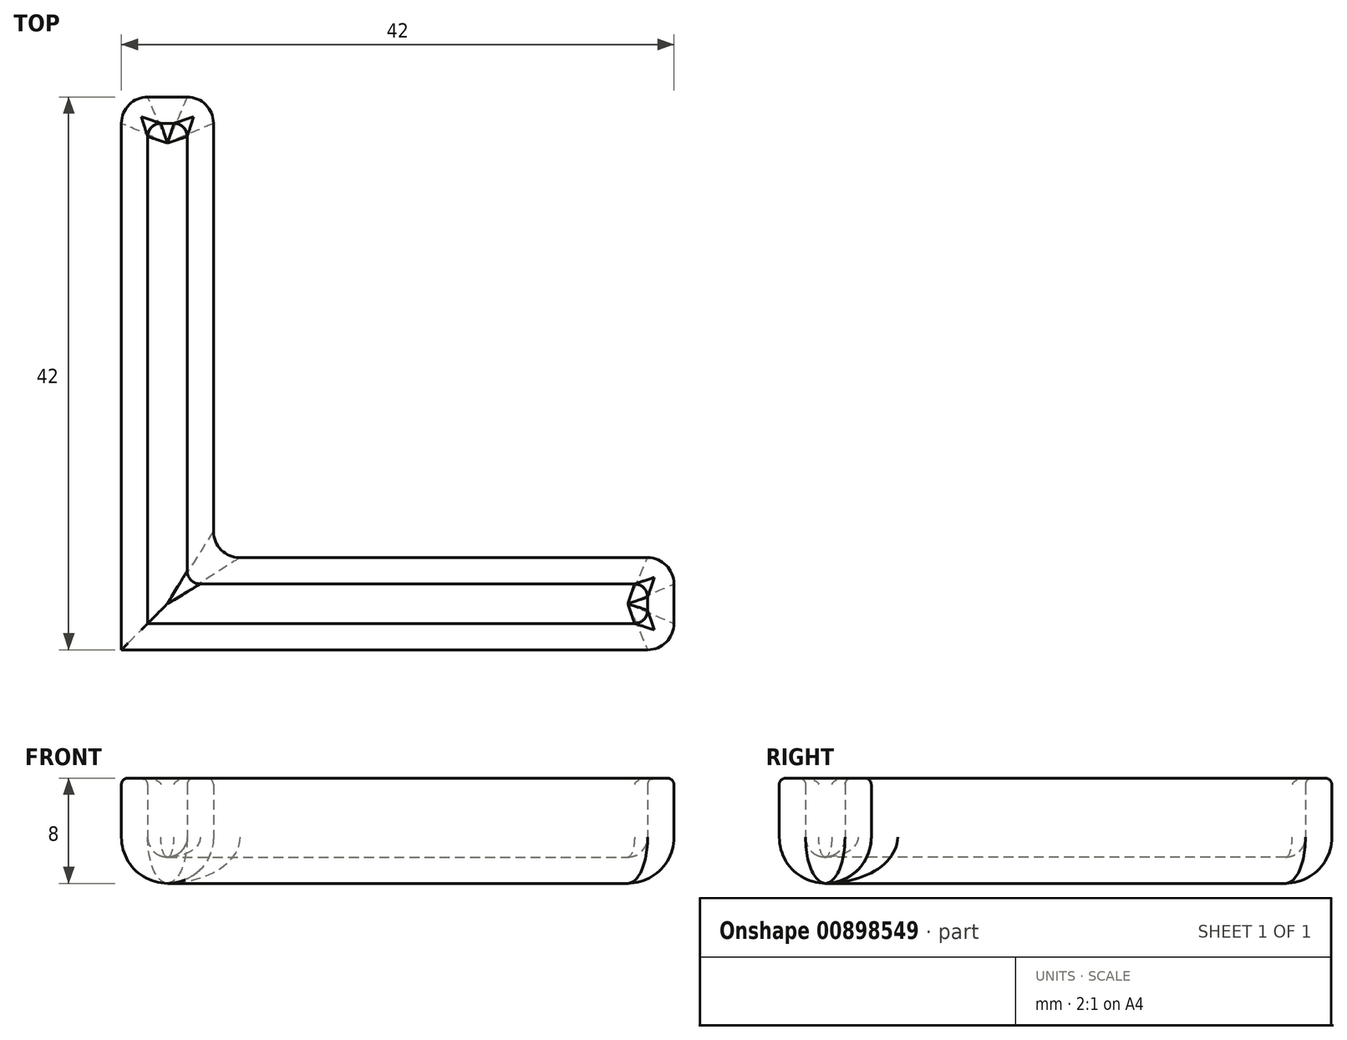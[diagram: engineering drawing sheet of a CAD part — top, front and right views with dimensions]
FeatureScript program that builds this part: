
annotation { "Feature Type Name" : "Feature", "Feature Type Description" : "" }
export const myFeature = defineFeature(function(context is Context, id is Id, definition is map)
    precondition{}
    {
        {
            var Q0;
            Q0=qCreatedBy(makeId("Top.planeOp"),FACE);
            var sketch = newSketch(context, id + "F0", { "sketchPlane" : qUnion([Q0])});
            skLineSegment(sketch, "E0.bottom", {"start": v(0.08, 0.3) * mm, "end": v(42.08, 0.3) * mm});
            skLineSegment(sketch, "E0.top", {"start": v(7.08, 7.3) * mm, "end": v(42.08, 7.3) * mm});
            skLineSegment(sketch, "E0.left", {"start": v(0.08, 0.3) * mm, "end": v(0.08, 7.3) * mm});
            skLineSegment(sketch, "E0.right", {"start": v(42.08, 0.3) * mm, "end": v(42.08, 7.3) * mm});
            skLineSegment(sketch, "E1.bottom", {"start": v(0.08, 0.3) * mm, "end": v(7.08, 0.3) * mm});
            skLineSegment(sketch, "E1.top", {"start": v(0.08, 42.3) * mm, "end": v(7.08, 42.3) * mm});
            skLineSegment(sketch, "E1.left", {"start": v(0.08, 0.3) * mm, "end": v(0.08, 42.3) * mm});
            skLineSegment(sketch, "E1.right", {"start": v(7.08, 7.3) * mm, "end": v(7.08, 42.3) * mm});
            skSolve(sketch);
        }
        {
            var Q0;
            Q0=makeQuery(id+"F0.imprint","IMPRINT",FACE,{"disambiguationData":[TD([[makeQuery(id+"F0.imprint","IMPRINT",EDGE,{"derivedFrom":sQuery(id+"F0.wireOp",EDGE,"E0.bottom")}),1.0]])]});
            extrude(context, id + "F1", {"entities" : qUnion([Q0]), "depth" : 6 * mm, "offsetDistance" : 25 * mm});
        }
        {
            var Q0;
            Q0=makeQuery(id+"F1.opExtrude","CAP_FACE",FACE,{"disambiguationData":[OSD([sQuery(id+"F0.wireOp",EDGE,"E0.bottom"),sQuery(id+"F0.wireOp",EDGE,"E0.top"),sQuery(id+"F0.wireOp",EDGE,"E0.right"),sQuery(id+"F0.wireOp",EDGE,"E1.bottom"),sQuery(id+"F0.wireOp",EDGE,"E1.top"),sQuery(id+"F0.wireOp",EDGE,"E1.left"),sQuery(id+"F0.wireOp",EDGE,"E1.right")])],"isStart":true});
            extrude(context, id + "F2", {"entities" : qUnion([Q0]), "operationType" : NewBodyOperationType.ADD, "depth" : 2 * mm, "offsetDistance" : 25 * mm});
        }
        {
            var Q0;
            Q0=makeQuery(id+"F2.opExtrude","CAP_EDGE",EDGE,{"disambiguationData":[OSD([sQuery(id+"F0.wireOp",EDGE,"E1.left")])],"isStart":false});
            var Q1;
            Q1=makeQuery(id+"F2.opExtrude","CAP_EDGE",EDGE,{"disambiguationData":[OSD([sQuery(id+"F0.wireOp",EDGE,"E1.top")])],"isStart":false});
            var Q2;
            Q2=makeQuery(id+"F2.opExtrude","CAP_EDGE",EDGE,{"disambiguationData":[OSD([sQuery(id+"F0.wireOp",EDGE,"E1.right")])],"isStart":false});
            var Q3;
            Q3=makeQuery(id+"F2.opExtrude","CAP_EDGE",EDGE,{"disambiguationData":[OSD([sQuery(id+"F0.wireOp",EDGE,"E0.top")])],"isStart":false});
            var Q4;
            Q4=makeQuery(id+"F2.opExtrude","CAP_EDGE",EDGE,{"disambiguationData":[OSD([sQuery(id+"F0.wireOp",EDGE,"E0.bottom"),sQuery(id+"F0.wireOp",EDGE,"E1.bottom")])],"isStart":false});
            var Q5;
            Q5=makeQuery(id+"F2.opExtrude","CAP_EDGE",EDGE,{"disambiguationData":[OSD([sQuery(id+"F0.wireOp",EDGE,"E0.right")])],"isStart":false});
            fillet(context, id + "F3", {"entities" : qUnion([Q0, Q1, Q2, Q3, Q4, Q5]), "radius" : 3.5 * mm, "tangentPropagation" : true, "allowEdgeOverflow" : false});
        }
        {
            var Q0;
            Q0=makeQuery(id+"F1.opExtrude","CAP_FACE",FACE,{"disambiguationData":[OSD([sQuery(id+"F0.wireOp",EDGE,"E0.bottom"),sQuery(id+"F0.wireOp",EDGE,"E0.top"),sQuery(id+"F0.wireOp",EDGE,"E0.right"),sQuery(id+"F0.wireOp",EDGE,"E1.bottom"),sQuery(id+"F0.wireOp",EDGE,"E1.top"),sQuery(id+"F0.wireOp",EDGE,"E1.left"),sQuery(id+"F0.wireOp",EDGE,"E1.right")])],"isStart":false});
            shell(context, id + "F4", {"entities" : qUnion([Q0]), "thickness" : 2 * mm});
        }
        {
            var Q0;
            {var subQ0=sQuery(id+"F0.wireOp",EDGE,"E0.right");var subQ1=sQuery(id+"F0.wireOp",EDGE,"E0.top");Q0=makeQuery(id+"F2.boolean.opBoolean","MERGE",EDGE,{"derivedFrom":[makeQuery(id+"F1.opExtrude","SWEPT_EDGE",EDGE,{"disambiguationData":[OSD([subQ1,subQ0])]}),makeQuery(id+"F2.opExtrude","SWEPT_EDGE",EDGE,{"disambiguationData":[OSD([subQ1,subQ0])]})]});}
            var Q1;
            {var subQ0=sQuery(id+"F0.wireOp",EDGE,"E0.right");var subQ1=sQuery(id+"F0.wireOp",EDGE,"E0.bottom");Q1=makeQuery(id+"F2.boolean.opBoolean","MERGE",EDGE,{"derivedFrom":[makeQuery(id+"F1.opExtrude","SWEPT_EDGE",EDGE,{"disambiguationData":[OSD([subQ1,subQ0])]}),makeQuery(id+"F2.opExtrude","SWEPT_EDGE",EDGE,{"disambiguationData":[OSD([subQ1,subQ0])]})]});}
            var Q2;
            {var subQ0=sQuery(id+"F0.wireOp",EDGE,"E1.left");var subQ1=sQuery(id+"F0.wireOp",EDGE,"E1.bottom");Q2=makeQuery(id+"F2.boolean.opBoolean","MERGE",EDGE,{"derivedFrom":[makeQuery(id+"F1.opExtrude","SWEPT_EDGE",EDGE,{"disambiguationData":[OSD([subQ1,subQ0])]}),makeQuery(id+"F2.opExtrude","SWEPT_EDGE",EDGE,{"disambiguationData":[OSD([subQ1,subQ0])]})]});}
            var Q3;
            {var subQ0=sQuery(id+"F0.wireOp",EDGE,"E1.right");var subQ1=sQuery(id+"F0.wireOp",EDGE,"E0.top");Q3=makeQuery(id+"F2.boolean.opBoolean","MERGE",EDGE,{"derivedFrom":[makeQuery(id+"F1.opExtrude","SWEPT_EDGE",EDGE,{"disambiguationData":[OSD([subQ1,subQ0])]}),makeQuery(id+"F2.opExtrude","SWEPT_EDGE",EDGE,{"disambiguationData":[OSD([subQ1,subQ0])]})]});}
            var Q4;
            {var subQ0=sQuery(id+"F0.wireOp",EDGE,"E1.right");var subQ1=sQuery(id+"F0.wireOp",EDGE,"E1.top");Q4=makeQuery(id+"F2.boolean.opBoolean","MERGE",EDGE,{"derivedFrom":[makeQuery(id+"F1.opExtrude","SWEPT_EDGE",EDGE,{"disambiguationData":[OSD([subQ1,subQ0])]}),makeQuery(id+"F2.opExtrude","SWEPT_EDGE",EDGE,{"disambiguationData":[OSD([subQ1,subQ0])]})]});}
            var Q5;
            {var subQ0=sQuery(id+"F0.wireOp",EDGE,"E1.left");var subQ1=sQuery(id+"F0.wireOp",EDGE,"E1.top");Q5=makeQuery(id+"F2.boolean.opBoolean","MERGE",EDGE,{"derivedFrom":[makeQuery(id+"F1.opExtrude","SWEPT_EDGE",EDGE,{"disambiguationData":[OSD([subQ1,subQ0])]}),makeQuery(id+"F2.opExtrude","SWEPT_EDGE",EDGE,{"disambiguationData":[OSD([subQ1,subQ0])]})]});}
            fillet(context, id + "F5", {"entities" : qUnion([Q0, Q1, Q2, Q3, Q4, Q5]), "radius" : 2 * mm, "tangentPropagation" : true, "allowEdgeOverflow" : false});
        }
        {
            var Q0;
            {var subQ0=sQuery(id+"F0.wireOp",EDGE,"E1.bottom");var subQ1=sQuery(id+"F0.wireOp",EDGE,"E0.bottom");Q0=makeQuery(id+"F4.opShell","OFFSET_EDGE",EDGE,{"disambiguationData":[OSD([subQ1,subQ0]),TDD([makeQuery(id+"F1.opExtrude","CAP_EDGE",EDGE,{"disambiguationData":[OSD([subQ1,subQ0])],"isStart":false})])]});}
            var Q1;
            {var subQ0=sQuery(id+"F0.wireOp",EDGE,"E1.left");var subQ1=sQuery(id+"F0.wireOp",EDGE,"E1.bottom");Q1=makeQuery(id+"FFNLwZtD0nWtF8N_1.opFillet","BLEND_EDGE",EDGE,{"blendedFrom":[makeQuery(id+"F4.opShell","OFFSET_EDGE",EDGE,{"disambiguationData":[OSD([subQ1,subQ0])]}),makeQuery(id+"F1.opExtrude","CAP_FACE",FACE,{"disambiguationData":[OSD([sQuery(id+"F0.wireOp",EDGE,"E0.bottom"),sQuery(id+"F0.wireOp",EDGE,"E0.top"),sQuery(id+"F0.wireOp",EDGE,"E0.right"),subQ1,sQuery(id+"F0.wireOp",EDGE,"E1.top"),subQ0,sQuery(id+"F0.wireOp",EDGE,"E1.right")])],"isStart":false})],"blendedInto":[makeQuery(id+"F1.opExtrude","CAP_FACE",FACE,{"disambiguationData":[OSD([sQuery(id+"F0.wireOp",EDGE,"E0.bottom"),sQuery(id+"F0.wireOp",EDGE,"E0.top"),sQuery(id+"F0.wireOp",EDGE,"E0.right"),subQ1,sQuery(id+"F0.wireOp",EDGE,"E1.top"),subQ0,sQuery(id+"F0.wireOp",EDGE,"E1.right")])],"isStart":false})]});}
            var Q2;
            {var subQ0=sQuery(id+"F0.wireOp",EDGE,"E1.left");Q2=makeQuery(id+"F4.opShell","OFFSET_EDGE",EDGE,{"disambiguationData":[OSD([subQ0]),TDD([makeQuery(id+"F1.opExtrude","CAP_EDGE",EDGE,{"disambiguationData":[OSD([subQ0])],"isStart":false})])]});}
            var Q3;
            {var subQ0=sQuery(id+"F0.wireOp",EDGE,"E1.right");Q3=makeQuery(id+"F4.opShell","OFFSET_EDGE",EDGE,{"disambiguationData":[OSD([subQ0]),TDD([makeQuery(id+"F1.opExtrude","CAP_EDGE",EDGE,{"disambiguationData":[OSD([subQ0])],"isStart":false})])]});}
            var Q4;
            {var subQ0=sQuery(id+"F0.wireOp",EDGE,"E1.right");var subQ1=sQuery(id+"F0.wireOp",EDGE,"E0.top");Q4=makeQuery(id+"FFNLwZtD0nWtF8N_1.opFillet","BLEND_EDGE",EDGE,{"blendedFrom":[makeQuery(id+"F4.opShell","OFFSET_EDGE",EDGE,{"disambiguationData":[OSD([subQ1,subQ0])]}),makeQuery(id+"F1.opExtrude","CAP_FACE",FACE,{"disambiguationData":[OSD([sQuery(id+"F0.wireOp",EDGE,"E0.bottom"),subQ1,sQuery(id+"F0.wireOp",EDGE,"E0.right"),sQuery(id+"F0.wireOp",EDGE,"E1.bottom"),sQuery(id+"F0.wireOp",EDGE,"E1.top"),sQuery(id+"F0.wireOp",EDGE,"E1.left"),subQ0])],"isStart":false})],"blendedInto":[makeQuery(id+"F1.opExtrude","CAP_FACE",FACE,{"disambiguationData":[OSD([sQuery(id+"F0.wireOp",EDGE,"E0.bottom"),subQ1,sQuery(id+"F0.wireOp",EDGE,"E0.right"),sQuery(id+"F0.wireOp",EDGE,"E1.bottom"),sQuery(id+"F0.wireOp",EDGE,"E1.top"),sQuery(id+"F0.wireOp",EDGE,"E1.left"),subQ0])],"isStart":false})]});}
            var Q5;
            {var subQ0=sQuery(id+"F0.wireOp",EDGE,"E0.top");Q5=makeQuery(id+"F4.opShell","OFFSET_EDGE",EDGE,{"disambiguationData":[OSD([subQ0]),TDD([makeQuery(id+"F1.opExtrude","CAP_EDGE",EDGE,{"disambiguationData":[OSD([subQ0])],"isStart":false})])]});}
            var Q6;
            {var subQ0=sQuery(id+"F0.wireOp",EDGE,"E0.right");var subQ1=sQuery(id+"F0.wireOp",EDGE,"E0.top");Q6=makeQuery(id+"FFNLwZtD0nWtF8N_1.opFillet","BLEND_EDGE",EDGE,{"blendedFrom":[makeQuery(id+"F4.opShell","OFFSET_EDGE",EDGE,{"disambiguationData":[OSD([subQ1,subQ0]),TDD([makeQuery(id+"F2.boolean.opBoolean","MERGE",EDGE,{"derivedFrom":[makeQuery(id+"F1.opExtrude","SWEPT_EDGE",EDGE,{"disambiguationData":[OSD([subQ1,subQ0])]}),makeQuery(id+"F2.opExtrude","SWEPT_EDGE",EDGE,{"disambiguationData":[OSD([subQ1,subQ0])]})]})])]}),makeQuery(id+"F1.opExtrude","CAP_FACE",FACE,{"disambiguationData":[OSD([sQuery(id+"F0.wireOp",EDGE,"E0.bottom"),subQ1,subQ0,sQuery(id+"F0.wireOp",EDGE,"E1.bottom"),sQuery(id+"F0.wireOp",EDGE,"E1.top"),sQuery(id+"F0.wireOp",EDGE,"E1.left"),sQuery(id+"F0.wireOp",EDGE,"E1.right")])],"isStart":false})],"blendedInto":[makeQuery(id+"F1.opExtrude","CAP_FACE",FACE,{"disambiguationData":[OSD([sQuery(id+"F0.wireOp",EDGE,"E0.bottom"),subQ1,subQ0,sQuery(id+"F0.wireOp",EDGE,"E1.bottom"),sQuery(id+"F0.wireOp",EDGE,"E1.top"),sQuery(id+"F0.wireOp",EDGE,"E1.left"),sQuery(id+"F0.wireOp",EDGE,"E1.right")])],"isStart":false})]});}
            var Q7;
            {var subQ0=sQuery(id+"F0.wireOp",EDGE,"E0.right");var subQ1=sQuery(id+"F0.wireOp",EDGE,"E0.bottom");Q7=makeQuery(id+"FFNLwZtD0nWtF8N_1.opFillet","BLEND_EDGE",EDGE,{"blendedFrom":[makeQuery(id+"F4.opShell","OFFSET_EDGE",EDGE,{"disambiguationData":[OSD([subQ1,subQ0])]}),makeQuery(id+"F1.opExtrude","CAP_FACE",FACE,{"disambiguationData":[OSD([subQ1,sQuery(id+"F0.wireOp",EDGE,"E0.top"),subQ0,sQuery(id+"F0.wireOp",EDGE,"E1.bottom"),sQuery(id+"F0.wireOp",EDGE,"E1.top"),sQuery(id+"F0.wireOp",EDGE,"E1.left"),sQuery(id+"F0.wireOp",EDGE,"E1.right")])],"isStart":false})],"blendedInto":[makeQuery(id+"F1.opExtrude","CAP_FACE",FACE,{"disambiguationData":[OSD([subQ1,sQuery(id+"F0.wireOp",EDGE,"E0.top"),subQ0,sQuery(id+"F0.wireOp",EDGE,"E1.bottom"),sQuery(id+"F0.wireOp",EDGE,"E1.top"),sQuery(id+"F0.wireOp",EDGE,"E1.left"),sQuery(id+"F0.wireOp",EDGE,"E1.right")])],"isStart":false})]});}
            var Q8;
            {var subQ0=sQuery(id+"F0.wireOp",EDGE,"E0.right");Q8=makeQuery(id+"F4.opShell","OFFSET_EDGE",EDGE,{"disambiguationData":[OSD([subQ0]),TDD([makeQuery(id+"F1.opExtrude","CAP_EDGE",EDGE,{"disambiguationData":[OSD([subQ0])],"isStart":false})])]});}
            var Q9;
            {var subQ0=sQuery(id+"F0.wireOp",EDGE,"E1.left");var subQ1=sQuery(id+"F0.wireOp",EDGE,"E1.top");Q9=makeQuery(id+"FFNLwZtD0nWtF8N_1.opFillet","BLEND_EDGE",EDGE,{"blendedFrom":[makeQuery(id+"F4.opShell","OFFSET_EDGE",EDGE,{"disambiguationData":[OSD([subQ1,subQ0]),TDD([makeQuery(id+"F2.boolean.opBoolean","MERGE",EDGE,{"derivedFrom":[makeQuery(id+"F1.opExtrude","SWEPT_EDGE",EDGE,{"disambiguationData":[OSD([subQ1,subQ0])]}),makeQuery(id+"F2.opExtrude","SWEPT_EDGE",EDGE,{"disambiguationData":[OSD([subQ1,subQ0])]})]})])]}),makeQuery(id+"F1.opExtrude","CAP_FACE",FACE,{"disambiguationData":[OSD([sQuery(id+"F0.wireOp",EDGE,"E0.bottom"),sQuery(id+"F0.wireOp",EDGE,"E0.top"),sQuery(id+"F0.wireOp",EDGE,"E0.right"),sQuery(id+"F0.wireOp",EDGE,"E1.bottom"),subQ1,subQ0,sQuery(id+"F0.wireOp",EDGE,"E1.right")])],"isStart":false})],"blendedInto":[makeQuery(id+"F1.opExtrude","CAP_FACE",FACE,{"disambiguationData":[OSD([sQuery(id+"F0.wireOp",EDGE,"E0.bottom"),sQuery(id+"F0.wireOp",EDGE,"E0.top"),sQuery(id+"F0.wireOp",EDGE,"E0.right"),sQuery(id+"F0.wireOp",EDGE,"E1.bottom"),subQ1,subQ0,sQuery(id+"F0.wireOp",EDGE,"E1.right")])],"isStart":false})]});}
            var Q10;
            {var subQ0=sQuery(id+"F0.wireOp",EDGE,"E1.top");Q10=makeQuery(id+"F4.opShell","OFFSET_EDGE",EDGE,{"disambiguationData":[OSD([subQ0]),TDD([makeQuery(id+"F1.opExtrude","CAP_EDGE",EDGE,{"disambiguationData":[OSD([subQ0])],"isStart":false})])]});}
            var Q11;
            {var subQ0=sQuery(id+"F0.wireOp",EDGE,"E1.right");var subQ1=sQuery(id+"F0.wireOp",EDGE,"E1.top");Q11=makeQuery(id+"FFNLwZtD0nWtF8N_1.opFillet","BLEND_EDGE",EDGE,{"blendedFrom":[makeQuery(id+"F4.opShell","OFFSET_EDGE",EDGE,{"disambiguationData":[OSD([subQ1,subQ0]),TDD([makeQuery(id+"F2.boolean.opBoolean","MERGE",EDGE,{"derivedFrom":[makeQuery(id+"F1.opExtrude","SWEPT_EDGE",EDGE,{"disambiguationData":[OSD([subQ1,subQ0])]}),makeQuery(id+"F2.opExtrude","SWEPT_EDGE",EDGE,{"disambiguationData":[OSD([subQ1,subQ0])]})]})])]}),makeQuery(id+"F1.opExtrude","CAP_FACE",FACE,{"disambiguationData":[OSD([sQuery(id+"F0.wireOp",EDGE,"E0.bottom"),sQuery(id+"F0.wireOp",EDGE,"E0.top"),sQuery(id+"F0.wireOp",EDGE,"E0.right"),sQuery(id+"F0.wireOp",EDGE,"E1.bottom"),subQ1,sQuery(id+"F0.wireOp",EDGE,"E1.left"),subQ0])],"isStart":false})],"blendedInto":[makeQuery(id+"F1.opExtrude","CAP_FACE",FACE,{"disambiguationData":[OSD([sQuery(id+"F0.wireOp",EDGE,"E0.bottom"),sQuery(id+"F0.wireOp",EDGE,"E0.top"),sQuery(id+"F0.wireOp",EDGE,"E0.right"),sQuery(id+"F0.wireOp",EDGE,"E1.bottom"),subQ1,sQuery(id+"F0.wireOp",EDGE,"E1.left"),subQ0])],"isStart":false})]});}
            var Q12;
            Q12=makeQuery(id+"F1.opExtrude","CAP_EDGE",EDGE,{"disambiguationData":[OSD([sQuery(id+"F0.wireOp",EDGE,"E1.left")])],"isStart":false});
            var Q13;
            Q13=makeQuery(id+"F1.opExtrude","CAP_EDGE",EDGE,{"disambiguationData":[OSD([sQuery(id+"F0.wireOp",EDGE,"E0.bottom"),sQuery(id+"F0.wireOp",EDGE,"E1.bottom")])],"isStart":false});
            var Q14;
            {var subQ0=sQuery(id+"F0.wireOp",EDGE,"E1.left");var subQ1=sQuery(id+"F0.wireOp",EDGE,"E1.bottom");Q14=makeQuery(id+"F5.opFillet","BLEND_EDGE",EDGE,{"blendedFrom":[makeQuery(id+"F2.boolean.opBoolean","MERGE",EDGE,{"derivedFrom":[makeQuery(id+"F1.opExtrude","SWEPT_EDGE",EDGE,{"disambiguationData":[OSD([subQ1,subQ0])]}),makeQuery(id+"F2.opExtrude","SWEPT_EDGE",EDGE,{"disambiguationData":[OSD([subQ1,subQ0])]})]}),makeQuery(id+"F1.opExtrude","CAP_FACE",FACE,{"disambiguationData":[OSD([sQuery(id+"F0.wireOp",EDGE,"E0.bottom"),sQuery(id+"F0.wireOp",EDGE,"E0.top"),sQuery(id+"F0.wireOp",EDGE,"E0.right"),subQ1,sQuery(id+"F0.wireOp",EDGE,"E1.top"),subQ0,sQuery(id+"F0.wireOp",EDGE,"E1.right")])],"isStart":false})],"blendedInto":[makeQuery(id+"F1.opExtrude","CAP_FACE",FACE,{"disambiguationData":[OSD([sQuery(id+"F0.wireOp",EDGE,"E0.bottom"),sQuery(id+"F0.wireOp",EDGE,"E0.top"),sQuery(id+"F0.wireOp",EDGE,"E0.right"),subQ1,sQuery(id+"F0.wireOp",EDGE,"E1.top"),subQ0,sQuery(id+"F0.wireOp",EDGE,"E1.right")])],"isStart":false})]});}
            var Q15;
            {var subQ0=sQuery(id+"F0.wireOp",EDGE,"E1.left");var subQ1=sQuery(id+"F0.wireOp",EDGE,"E1.top");Q15=makeQuery(id+"F5.opFillet","BLEND_EDGE",EDGE,{"blendedFrom":[makeQuery(id+"F2.boolean.opBoolean","MERGE",EDGE,{"derivedFrom":[makeQuery(id+"F1.opExtrude","SWEPT_EDGE",EDGE,{"disambiguationData":[OSD([subQ1,subQ0])]}),makeQuery(id+"F2.opExtrude","SWEPT_EDGE",EDGE,{"disambiguationData":[OSD([subQ1,subQ0])]})]}),makeQuery(id+"F1.opExtrude","CAP_FACE",FACE,{"disambiguationData":[OSD([sQuery(id+"F0.wireOp",EDGE,"E0.bottom"),sQuery(id+"F0.wireOp",EDGE,"E0.top"),sQuery(id+"F0.wireOp",EDGE,"E0.right"),sQuery(id+"F0.wireOp",EDGE,"E1.bottom"),subQ1,subQ0,sQuery(id+"F0.wireOp",EDGE,"E1.right")])],"isStart":false})],"blendedInto":[makeQuery(id+"F1.opExtrude","CAP_FACE",FACE,{"disambiguationData":[OSD([sQuery(id+"F0.wireOp",EDGE,"E0.bottom"),sQuery(id+"F0.wireOp",EDGE,"E0.top"),sQuery(id+"F0.wireOp",EDGE,"E0.right"),sQuery(id+"F0.wireOp",EDGE,"E1.bottom"),subQ1,subQ0,sQuery(id+"F0.wireOp",EDGE,"E1.right")])],"isStart":false})]});}
            var Q16;
            Q16=makeQuery(id+"F1.opExtrude","CAP_EDGE",EDGE,{"disambiguationData":[OSD([sQuery(id+"F0.wireOp",EDGE,"E1.top")])],"isStart":false});
            var Q17;
            {var subQ0=sQuery(id+"F0.wireOp",EDGE,"E1.right");var subQ1=sQuery(id+"F0.wireOp",EDGE,"E1.top");Q17=makeQuery(id+"F5.opFillet","BLEND_EDGE",EDGE,{"blendedFrom":[makeQuery(id+"F2.boolean.opBoolean","MERGE",EDGE,{"derivedFrom":[makeQuery(id+"F1.opExtrude","SWEPT_EDGE",EDGE,{"disambiguationData":[OSD([subQ1,subQ0])]}),makeQuery(id+"F2.opExtrude","SWEPT_EDGE",EDGE,{"disambiguationData":[OSD([subQ1,subQ0])]})]}),makeQuery(id+"F1.opExtrude","CAP_FACE",FACE,{"disambiguationData":[OSD([sQuery(id+"F0.wireOp",EDGE,"E0.bottom"),sQuery(id+"F0.wireOp",EDGE,"E0.top"),sQuery(id+"F0.wireOp",EDGE,"E0.right"),sQuery(id+"F0.wireOp",EDGE,"E1.bottom"),subQ1,sQuery(id+"F0.wireOp",EDGE,"E1.left"),subQ0])],"isStart":false})],"blendedInto":[makeQuery(id+"F1.opExtrude","CAP_FACE",FACE,{"disambiguationData":[OSD([sQuery(id+"F0.wireOp",EDGE,"E0.bottom"),sQuery(id+"F0.wireOp",EDGE,"E0.top"),sQuery(id+"F0.wireOp",EDGE,"E0.right"),sQuery(id+"F0.wireOp",EDGE,"E1.bottom"),subQ1,sQuery(id+"F0.wireOp",EDGE,"E1.left"),subQ0])],"isStart":false})]});}
            var Q18;
            Q18=makeQuery(id+"F1.opExtrude","CAP_EDGE",EDGE,{"disambiguationData":[OSD([sQuery(id+"F0.wireOp",EDGE,"E1.right")])],"isStart":false});
            var Q19;
            {var subQ0=sQuery(id+"F0.wireOp",EDGE,"E1.right");var subQ1=sQuery(id+"F0.wireOp",EDGE,"E0.top");Q19=makeQuery(id+"F5.opFillet","BLEND_EDGE",EDGE,{"blendedFrom":[makeQuery(id+"F2.boolean.opBoolean","MERGE",EDGE,{"derivedFrom":[makeQuery(id+"F1.opExtrude","SWEPT_EDGE",EDGE,{"disambiguationData":[OSD([subQ1,subQ0])]}),makeQuery(id+"F2.opExtrude","SWEPT_EDGE",EDGE,{"disambiguationData":[OSD([subQ1,subQ0])]})]}),makeQuery(id+"F1.opExtrude","CAP_FACE",FACE,{"disambiguationData":[OSD([sQuery(id+"F0.wireOp",EDGE,"E0.bottom"),subQ1,sQuery(id+"F0.wireOp",EDGE,"E0.right"),sQuery(id+"F0.wireOp",EDGE,"E1.bottom"),sQuery(id+"F0.wireOp",EDGE,"E1.top"),sQuery(id+"F0.wireOp",EDGE,"E1.left"),subQ0])],"isStart":false})],"blendedInto":[makeQuery(id+"F1.opExtrude","CAP_FACE",FACE,{"disambiguationData":[OSD([sQuery(id+"F0.wireOp",EDGE,"E0.bottom"),subQ1,sQuery(id+"F0.wireOp",EDGE,"E0.right"),sQuery(id+"F0.wireOp",EDGE,"E1.bottom"),sQuery(id+"F0.wireOp",EDGE,"E1.top"),sQuery(id+"F0.wireOp",EDGE,"E1.left"),subQ0])],"isStart":false})]});}
            var Q20;
            Q20=makeQuery(id+"F1.opExtrude","CAP_EDGE",EDGE,{"disambiguationData":[OSD([sQuery(id+"F0.wireOp",EDGE,"E0.top")])],"isStart":false});
            var Q21;
            {var subQ0=sQuery(id+"F0.wireOp",EDGE,"E0.right");var subQ1=sQuery(id+"F0.wireOp",EDGE,"E0.top");Q21=makeQuery(id+"F5.opFillet","BLEND_EDGE",EDGE,{"blendedFrom":[makeQuery(id+"F2.boolean.opBoolean","MERGE",EDGE,{"derivedFrom":[makeQuery(id+"F1.opExtrude","SWEPT_EDGE",EDGE,{"disambiguationData":[OSD([subQ1,subQ0])]}),makeQuery(id+"F2.opExtrude","SWEPT_EDGE",EDGE,{"disambiguationData":[OSD([subQ1,subQ0])]})]}),makeQuery(id+"F1.opExtrude","CAP_FACE",FACE,{"disambiguationData":[OSD([sQuery(id+"F0.wireOp",EDGE,"E0.bottom"),subQ1,subQ0,sQuery(id+"F0.wireOp",EDGE,"E1.bottom"),sQuery(id+"F0.wireOp",EDGE,"E1.top"),sQuery(id+"F0.wireOp",EDGE,"E1.left"),sQuery(id+"F0.wireOp",EDGE,"E1.right")])],"isStart":false})],"blendedInto":[makeQuery(id+"F1.opExtrude","CAP_FACE",FACE,{"disambiguationData":[OSD([sQuery(id+"F0.wireOp",EDGE,"E0.bottom"),subQ1,subQ0,sQuery(id+"F0.wireOp",EDGE,"E1.bottom"),sQuery(id+"F0.wireOp",EDGE,"E1.top"),sQuery(id+"F0.wireOp",EDGE,"E1.left"),sQuery(id+"F0.wireOp",EDGE,"E1.right")])],"isStart":false})]});}
            var Q22;
            Q22=makeQuery(id+"F1.opExtrude","CAP_EDGE",EDGE,{"disambiguationData":[OSD([sQuery(id+"F0.wireOp",EDGE,"E0.right")])],"isStart":false});
            var Q23;
            {var subQ0=sQuery(id+"F0.wireOp",EDGE,"E0.right");var subQ1=sQuery(id+"F0.wireOp",EDGE,"E0.bottom");Q23=makeQuery(id+"F5.opFillet","BLEND_EDGE",EDGE,{"blendedFrom":[makeQuery(id+"F2.boolean.opBoolean","MERGE",EDGE,{"derivedFrom":[makeQuery(id+"F1.opExtrude","SWEPT_EDGE",EDGE,{"disambiguationData":[OSD([subQ1,subQ0])]}),makeQuery(id+"F2.opExtrude","SWEPT_EDGE",EDGE,{"disambiguationData":[OSD([subQ1,subQ0])]})]}),makeQuery(id+"F1.opExtrude","CAP_FACE",FACE,{"disambiguationData":[OSD([subQ1,sQuery(id+"F0.wireOp",EDGE,"E0.top"),subQ0,sQuery(id+"F0.wireOp",EDGE,"E1.bottom"),sQuery(id+"F0.wireOp",EDGE,"E1.top"),sQuery(id+"F0.wireOp",EDGE,"E1.left"),sQuery(id+"F0.wireOp",EDGE,"E1.right")])],"isStart":false})],"blendedInto":[makeQuery(id+"F1.opExtrude","CAP_FACE",FACE,{"disambiguationData":[OSD([subQ1,sQuery(id+"F0.wireOp",EDGE,"E0.top"),subQ0,sQuery(id+"F0.wireOp",EDGE,"E1.bottom"),sQuery(id+"F0.wireOp",EDGE,"E1.top"),sQuery(id+"F0.wireOp",EDGE,"E1.left"),sQuery(id+"F0.wireOp",EDGE,"E1.right")])],"isStart":false})]});}
            fillet(context, id + "F6", {"entities" : qUnion([Q0, Q1, Q2, Q3, Q4, Q5, Q6, Q7, Q8, Q9, Q10, Q11, Q12, Q13, Q14, Q15, Q16, Q17, Q18, Q19, Q20, Q21, Q22, Q23]), "radius" : .5 * mm, "tangentPropagation" : true, "allowEdgeOverflow" : false});
        }
        {
            var Q0;
            Q0=makeQuery(id+"F4.opShell","OFFSET_EDGE",EDGE,{"disambiguationData":[OSD([sQuery(id+"F0.wireOp",EDGE,"E0.top"),sQuery(id+"F0.wireOp",EDGE,"E1.right")])]});
            var Q1;
            Q1=makeQuery(id+"F4.opShell","OFFSET_EDGE",EDGE,{"disambiguationData":[OSD([sQuery(id+"F0.wireOp",EDGE,"E1.bottom"),sQuery(id+"F0.wireOp",EDGE,"E1.left")])]});
            fillet(context, id + "F7", {"entities" : qUnion([Q0, Q1]), "radius" : 1 * mm, "tangentPropagation" : true, "allowEdgeOverflow" : false});
        }
        {
            var Q0;
            {var subQ0=sQuery(id+"F0.wireOp",EDGE,"E1.left");var subQ1=sQuery(id+"F0.wireOp",EDGE,"E1.top");Q0=makeQuery(id+"F4.opShell","OFFSET_EDGE",EDGE,{"disambiguationData":[OSD([subQ1,subQ0]),TDD([makeQuery(id+"F2.boolean.opBoolean","MERGE",EDGE,{"derivedFrom":[makeQuery(id+"F1.opExtrude","SWEPT_EDGE",EDGE,{"disambiguationData":[OSD([subQ1,subQ0])]}),makeQuery(id+"F2.opExtrude","SWEPT_EDGE",EDGE,{"disambiguationData":[OSD([subQ1,subQ0])]})]})])]});}
            var Q1;
            {var subQ0=sQuery(id+"F0.wireOp",EDGE,"E1.right");var subQ1=sQuery(id+"F0.wireOp",EDGE,"E1.top");Q1=makeQuery(id+"F4.opShell","OFFSET_EDGE",EDGE,{"disambiguationData":[OSD([subQ1,subQ0]),TDD([makeQuery(id+"F2.boolean.opBoolean","MERGE",EDGE,{"derivedFrom":[makeQuery(id+"F1.opExtrude","SWEPT_EDGE",EDGE,{"disambiguationData":[OSD([subQ1,subQ0])]}),makeQuery(id+"F2.opExtrude","SWEPT_EDGE",EDGE,{"disambiguationData":[OSD([subQ1,subQ0])]})]})])]});}
            var Q2;
            {var subQ0=sQuery(id+"F0.wireOp",EDGE,"E0.right");var subQ1=sQuery(id+"F0.wireOp",EDGE,"E0.top");Q2=makeQuery(id+"F4.opShell","OFFSET_EDGE",EDGE,{"disambiguationData":[OSD([subQ1,subQ0]),TDD([makeQuery(id+"F2.boolean.opBoolean","MERGE",EDGE,{"derivedFrom":[makeQuery(id+"F1.opExtrude","SWEPT_EDGE",EDGE,{"disambiguationData":[OSD([subQ1,subQ0])]}),makeQuery(id+"F2.opExtrude","SWEPT_EDGE",EDGE,{"disambiguationData":[OSD([subQ1,subQ0])]})]})])]});}
            var Q3;
            Q3=makeQuery(id+"F4.opShell","OFFSET_EDGE",EDGE,{"disambiguationData":[OSD([sQuery(id+"F0.wireOp",EDGE,"E0.bottom"),sQuery(id+"F0.wireOp",EDGE,"E0.right")])]});
            fillet(context, id + "F8", {"entities" : qUnion([Q0, Q1, Q2, Q3]), "radius" : 1 * mm, "tangentPropagation" : true, "allowEdgeOverflow" : false});
        }
    });
